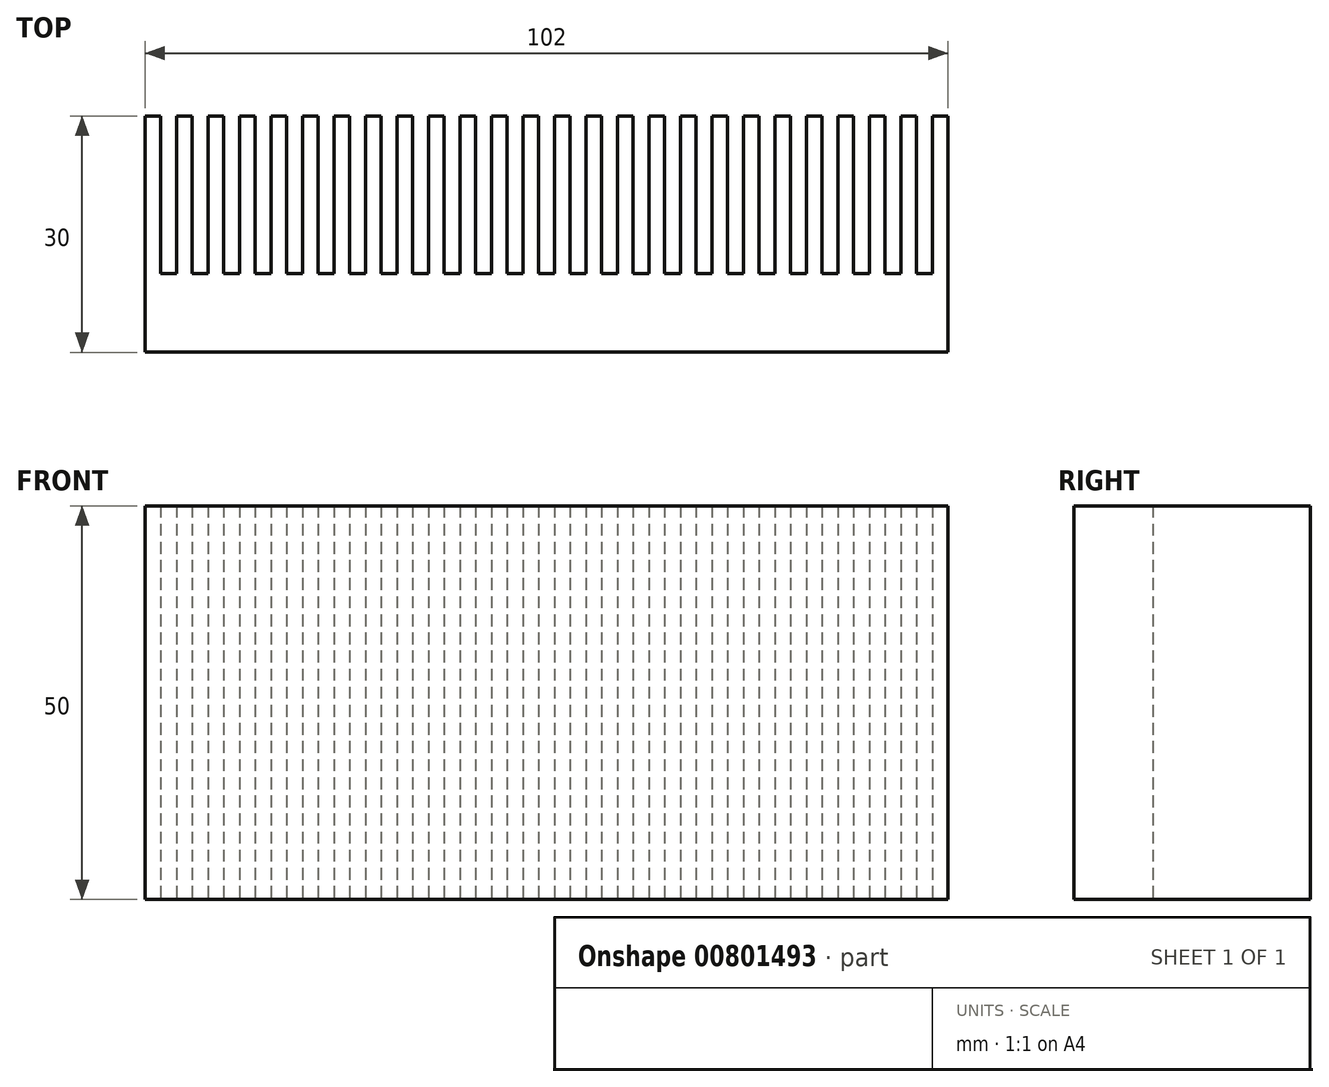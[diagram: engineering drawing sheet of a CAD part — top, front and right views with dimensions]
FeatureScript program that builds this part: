
annotation { "Feature Type Name" : "Feature", "Feature Type Description" : "" }
export const myFeature = defineFeature(function(context is Context, id is Id, definition is map)
    precondition{}
    {
        {
            var Q0;
            Q0=qCreatedBy(makeId("Top.planeOp"),FACE);
            var sketch = newSketch(context, id + "F0", { "sketchPlane" : qUnion([Q0])});
            skLineSegment(sketch, "E0", {"start": v(-567.65, -272.97) * mm, "end": v(-465.65, -272.97) * mm});
            skLineSegment(sketch, "E1", {"start": v(-465.65, -272.97) * mm, "end": v(-465.65, -242.97) * mm});
            skLineSegment(sketch, "E2", {"start": v(-465.65, -242.97) * mm, "end": v(-467.65, -242.97) * mm});
            skLineSegment(sketch, "E3", {"start": v(-467.65, -242.97) * mm, "end": v(-467.65, -262.97) * mm});
            skLineSegment(sketch, "E4", {"start": v(-467.65, -262.97) * mm, "end": v(-469.65, -262.97) * mm});
            skLineSegment(sketch, "E5", {"start": v(-469.65, -262.97) * mm, "end": v(-469.65, -242.97) * mm});
            skLineSegment(sketch, "E6.1.0.0", {"start": v(-469.65, -242.97) * mm, "end": v(-471.65, -242.97) * mm});
            skLineSegment(sketch, "E6.1.0.1", {"start": v(-471.65, -242.97) * mm, "end": v(-471.65, -262.97) * mm});
            skLineSegment(sketch, "E6.1.0.2", {"start": v(-471.65, -262.97) * mm, "end": v(-473.65, -262.97) * mm});
            skLineSegment(sketch, "E6.1.0.3", {"start": v(-473.65, -262.97) * mm, "end": v(-473.65, -242.97) * mm});
            skLineSegment(sketch, "E6.2.0.0", {"start": v(-473.65, -242.97) * mm, "end": v(-475.65, -242.97) * mm});
            skLineSegment(sketch, "E6.2.0.1", {"start": v(-475.65, -242.97) * mm, "end": v(-475.65, -262.97) * mm});
            skLineSegment(sketch, "E6.2.0.2", {"start": v(-475.65, -262.97) * mm, "end": v(-477.65, -262.97) * mm});
            skLineSegment(sketch, "E6.2.0.3", {"start": v(-477.65, -262.97) * mm, "end": v(-477.65, -242.97) * mm});
            skLineSegment(sketch, "E6.3.0.0", {"start": v(-477.65, -242.97) * mm, "end": v(-479.65, -242.97) * mm});
            skLineSegment(sketch, "E6.3.0.1", {"start": v(-479.65, -242.97) * mm, "end": v(-479.65, -262.97) * mm});
            skLineSegment(sketch, "E6.3.0.2", {"start": v(-479.65, -262.97) * mm, "end": v(-481.65, -262.97) * mm});
            skLineSegment(sketch, "E6.3.0.3", {"start": v(-481.65, -262.97) * mm, "end": v(-481.65, -242.97) * mm});
            skLineSegment(sketch, "E6.4.0.0", {"start": v(-481.65, -242.97) * mm, "end": v(-483.65, -242.97) * mm});
            skLineSegment(sketch, "E6.4.0.1", {"start": v(-483.65, -242.97) * mm, "end": v(-483.65, -262.97) * mm});
            skLineSegment(sketch, "E6.4.0.2", {"start": v(-483.65, -262.97) * mm, "end": v(-485.65, -262.97) * mm});
            skLineSegment(sketch, "E6.4.0.3", {"start": v(-485.65, -262.97) * mm, "end": v(-485.65, -242.97) * mm});
            skLineSegment(sketch, "E6.5.0.0", {"start": v(-485.65, -242.97) * mm, "end": v(-487.65, -242.97) * mm});
            skLineSegment(sketch, "E6.5.0.1", {"start": v(-487.65, -242.97) * mm, "end": v(-487.65, -262.97) * mm});
            skLineSegment(sketch, "E6.5.0.2", {"start": v(-487.65, -262.97) * mm, "end": v(-489.65, -262.97) * mm});
            skLineSegment(sketch, "E6.5.0.3", {"start": v(-489.65, -262.97) * mm, "end": v(-489.65, -242.97) * mm});
            skLineSegment(sketch, "E6.6.0.0", {"start": v(-489.65, -242.97) * mm, "end": v(-491.65, -242.97) * mm});
            skLineSegment(sketch, "E6.6.0.1", {"start": v(-491.65, -242.97) * mm, "end": v(-491.65, -262.97) * mm});
            skLineSegment(sketch, "E6.6.0.2", {"start": v(-491.65, -262.97) * mm, "end": v(-493.65, -262.97) * mm});
            skLineSegment(sketch, "E6.6.0.3", {"start": v(-493.65, -262.97) * mm, "end": v(-493.65, -242.97) * mm});
            skLineSegment(sketch, "E6.7.0.0", {"start": v(-493.65, -242.97) * mm, "end": v(-495.65, -242.97) * mm});
            skLineSegment(sketch, "E6.7.0.1", {"start": v(-495.65, -242.97) * mm, "end": v(-495.65, -262.97) * mm});
            skLineSegment(sketch, "E6.7.0.2", {"start": v(-495.65, -262.97) * mm, "end": v(-497.65, -262.97) * mm});
            skLineSegment(sketch, "E6.7.0.3", {"start": v(-497.65, -262.97) * mm, "end": v(-497.65, -242.97) * mm});
            skLineSegment(sketch, "E6.8.0.0", {"start": v(-497.65, -242.97) * mm, "end": v(-499.65, -242.97) * mm});
            skLineSegment(sketch, "E6.8.0.1", {"start": v(-499.65, -242.97) * mm, "end": v(-499.65, -262.97) * mm});
            skLineSegment(sketch, "E6.8.0.2", {"start": v(-499.65, -262.97) * mm, "end": v(-501.65, -262.97) * mm});
            skLineSegment(sketch, "E6.8.0.3", {"start": v(-501.65, -262.97) * mm, "end": v(-501.65, -242.97) * mm});
            skLineSegment(sketch, "E6.9.0.0", {"start": v(-501.65, -242.97) * mm, "end": v(-503.65, -242.97) * mm});
            skLineSegment(sketch, "E6.9.0.1", {"start": v(-503.65, -242.97) * mm, "end": v(-503.65, -262.97) * mm});
            skLineSegment(sketch, "E6.9.0.2", {"start": v(-503.65, -262.97) * mm, "end": v(-505.65, -262.97) * mm});
            skLineSegment(sketch, "E6.9.0.3", {"start": v(-505.65, -262.97) * mm, "end": v(-505.65, -242.97) * mm});
            skLineSegment(sketch, "E6.10.0.0", {"start": v(-505.65, -242.97) * mm, "end": v(-507.65, -242.97) * mm});
            skLineSegment(sketch, "E6.10.0.1", {"start": v(-507.65, -242.97) * mm, "end": v(-507.65, -262.97) * mm});
            skLineSegment(sketch, "E6.10.0.2", {"start": v(-507.65, -262.97) * mm, "end": v(-509.65, -262.97) * mm});
            skLineSegment(sketch, "E6.10.0.3", {"start": v(-509.65, -262.97) * mm, "end": v(-509.65, -242.97) * mm});
            skLineSegment(sketch, "E6.11.0.0", {"start": v(-509.65, -242.97) * mm, "end": v(-511.65, -242.97) * mm});
            skLineSegment(sketch, "E6.11.0.1", {"start": v(-511.65, -242.97) * mm, "end": v(-511.65, -262.97) * mm});
            skLineSegment(sketch, "E6.11.0.2", {"start": v(-511.65, -262.97) * mm, "end": v(-513.65, -262.97) * mm});
            skLineSegment(sketch, "E6.11.0.3", {"start": v(-513.65, -262.97) * mm, "end": v(-513.65, -242.97) * mm});
            skLineSegment(sketch, "E6.12.0.0", {"start": v(-513.65, -242.97) * mm, "end": v(-515.65, -242.97) * mm});
            skLineSegment(sketch, "E6.12.0.1", {"start": v(-515.65, -242.97) * mm, "end": v(-515.65, -262.97) * mm});
            skLineSegment(sketch, "E6.12.0.2", {"start": v(-515.65, -262.97) * mm, "end": v(-517.65, -262.97) * mm});
            skLineSegment(sketch, "E6.12.0.3", {"start": v(-517.65, -262.97) * mm, "end": v(-517.65, -242.97) * mm});
            skLineSegment(sketch, "E6.13.0.0", {"start": v(-517.65, -242.97) * mm, "end": v(-519.65, -242.97) * mm});
            skLineSegment(sketch, "E6.13.0.1", {"start": v(-519.65, -242.97) * mm, "end": v(-519.65, -262.97) * mm});
            skLineSegment(sketch, "E6.13.0.2", {"start": v(-519.65, -262.97) * mm, "end": v(-521.65, -262.97) * mm});
            skLineSegment(sketch, "E6.13.0.3", {"start": v(-521.65, -262.97) * mm, "end": v(-521.65, -242.97) * mm});
            skLineSegment(sketch, "E6.14.0.0", {"start": v(-521.65, -242.97) * mm, "end": v(-523.65, -242.97) * mm});
            skLineSegment(sketch, "E6.14.0.1", {"start": v(-523.65, -242.97) * mm, "end": v(-523.65, -262.97) * mm});
            skLineSegment(sketch, "E6.14.0.2", {"start": v(-523.65, -262.97) * mm, "end": v(-525.65, -262.97) * mm});
            skLineSegment(sketch, "E6.14.0.3", {"start": v(-525.65, -262.97) * mm, "end": v(-525.65, -242.97) * mm});
            skLineSegment(sketch, "E6.15.0.0", {"start": v(-525.65, -242.97) * mm, "end": v(-527.65, -242.97) * mm});
            skLineSegment(sketch, "E6.15.0.1", {"start": v(-527.65, -242.97) * mm, "end": v(-527.65, -262.97) * mm});
            skLineSegment(sketch, "E6.15.0.2", {"start": v(-527.65, -262.97) * mm, "end": v(-529.65, -262.97) * mm});
            skLineSegment(sketch, "E6.15.0.3", {"start": v(-529.65, -262.97) * mm, "end": v(-529.65, -242.97) * mm});
            skLineSegment(sketch, "E6.16.0.0", {"start": v(-529.65, -242.97) * mm, "end": v(-531.65, -242.97) * mm});
            skLineSegment(sketch, "E6.16.0.1", {"start": v(-531.65, -242.97) * mm, "end": v(-531.65, -262.97) * mm});
            skLineSegment(sketch, "E6.16.0.2", {"start": v(-531.65, -262.97) * mm, "end": v(-533.65, -262.97) * mm});
            skLineSegment(sketch, "E6.16.0.3", {"start": v(-533.65, -262.97) * mm, "end": v(-533.65, -242.97) * mm});
            skLineSegment(sketch, "E6.17.0.0", {"start": v(-533.65, -242.97) * mm, "end": v(-535.65, -242.97) * mm});
            skLineSegment(sketch, "E6.17.0.1", {"start": v(-535.65, -242.97) * mm, "end": v(-535.65, -262.97) * mm});
            skLineSegment(sketch, "E6.17.0.2", {"start": v(-535.65, -262.97) * mm, "end": v(-537.65, -262.97) * mm});
            skLineSegment(sketch, "E6.17.0.3", {"start": v(-537.65, -262.97) * mm, "end": v(-537.65, -242.97) * mm});
            skLineSegment(sketch, "E6.18.0.0", {"start": v(-537.65, -242.97) * mm, "end": v(-539.65, -242.97) * mm});
            skLineSegment(sketch, "E6.18.0.1", {"start": v(-539.65, -242.97) * mm, "end": v(-539.65, -262.97) * mm});
            skLineSegment(sketch, "E6.18.0.2", {"start": v(-539.65, -262.97) * mm, "end": v(-541.65, -262.97) * mm});
            skLineSegment(sketch, "E6.18.0.3", {"start": v(-541.65, -262.97) * mm, "end": v(-541.65, -242.97) * mm});
            skLineSegment(sketch, "E6.19.0.0", {"start": v(-541.65, -242.97) * mm, "end": v(-543.65, -242.97) * mm});
            skLineSegment(sketch, "E6.19.0.1", {"start": v(-543.65, -242.97) * mm, "end": v(-543.65, -262.97) * mm});
            skLineSegment(sketch, "E6.19.0.2", {"start": v(-543.65, -262.97) * mm, "end": v(-545.65, -262.97) * mm});
            skLineSegment(sketch, "E6.19.0.3", {"start": v(-545.65, -262.97) * mm, "end": v(-545.65, -242.97) * mm});
            skLineSegment(sketch, "E6.20.0.0", {"start": v(-545.65, -242.97) * mm, "end": v(-547.65, -242.97) * mm});
            skLineSegment(sketch, "E6.20.0.1", {"start": v(-547.65, -242.97) * mm, "end": v(-547.65, -262.97) * mm});
            skLineSegment(sketch, "E6.20.0.2", {"start": v(-547.65, -262.97) * mm, "end": v(-549.65, -262.97) * mm});
            skLineSegment(sketch, "E6.20.0.3", {"start": v(-549.65, -262.97) * mm, "end": v(-549.65, -242.97) * mm});
            skLineSegment(sketch, "E6.21.0.0", {"start": v(-549.65, -242.97) * mm, "end": v(-551.65, -242.97) * mm});
            skLineSegment(sketch, "E6.21.0.1", {"start": v(-551.65, -242.97) * mm, "end": v(-551.65, -262.97) * mm});
            skLineSegment(sketch, "E6.21.0.2", {"start": v(-551.65, -262.97) * mm, "end": v(-553.65, -262.97) * mm});
            skLineSegment(sketch, "E6.21.0.3", {"start": v(-553.65, -262.97) * mm, "end": v(-553.65, -242.97) * mm});
            skLineSegment(sketch, "E6.22.0.0", {"start": v(-553.65, -242.97) * mm, "end": v(-555.65, -242.97) * mm});
            skLineSegment(sketch, "E6.22.0.1", {"start": v(-555.65, -242.97) * mm, "end": v(-555.65, -262.97) * mm});
            skLineSegment(sketch, "E6.22.0.2", {"start": v(-555.65, -262.97) * mm, "end": v(-557.65, -262.97) * mm});
            skLineSegment(sketch, "E6.22.0.3", {"start": v(-557.65, -262.97) * mm, "end": v(-557.65, -242.97) * mm});
            skLineSegment(sketch, "E6.23.0.0", {"start": v(-557.65, -242.97) * mm, "end": v(-559.65, -242.97) * mm});
            skLineSegment(sketch, "E6.23.0.1", {"start": v(-559.65, -242.97) * mm, "end": v(-559.65, -262.97) * mm});
            skLineSegment(sketch, "E6.23.0.2", {"start": v(-559.65, -262.97) * mm, "end": v(-561.65, -262.97) * mm});
            skLineSegment(sketch, "E6.23.0.3", {"start": v(-561.65, -262.97) * mm, "end": v(-561.65, -242.97) * mm});
            skLineSegment(sketch, "E6.24.0.0", {"start": v(-561.65, -242.97) * mm, "end": v(-563.65, -242.97) * mm});
            skLineSegment(sketch, "E6.24.0.1", {"start": v(-563.65, -242.97) * mm, "end": v(-563.65, -262.97) * mm});
            skLineSegment(sketch, "E6.24.0.2", {"start": v(-563.65, -262.97) * mm, "end": v(-565.65, -262.97) * mm});
            skLineSegment(sketch, "E6.direction1", {"start": v(-467.65, -242.97) * mm, "end": v(-471.65, -242.97) * mm, "construction": true});
            skLineSegment(sketch, "E7", {"start": v(-567.65, -272.97) * mm, "end": v(-567.65, -242.97) * mm});
            skLineSegment(sketch, "E8", {"start": v(-567.65, -242.97) * mm, "end": v(-565.65, -242.97) * mm});
            skLineSegment(sketch, "E9", {"start": v(-565.65, -262.97) * mm, "end": v(-565.65, -242.97) * mm});
            skSolve(sketch);
        }
        {
            var Q0;
            Q0=makeQuery(id+"F0.imprint","IMPRINT",FACE,{"disambiguationData":[TD([[makeQuery(id+"F0.imprint","IMPRINT",EDGE,{"derivedFrom":sQuery(id+"F0.wireOp",EDGE,"E0")}),1.0]])]});
            extrude(context, id + "F1", {"entities" : qUnion([Q0]), "depth" : 50 * mm, "offsetDistance" : 25 * mm});
        }
    });
